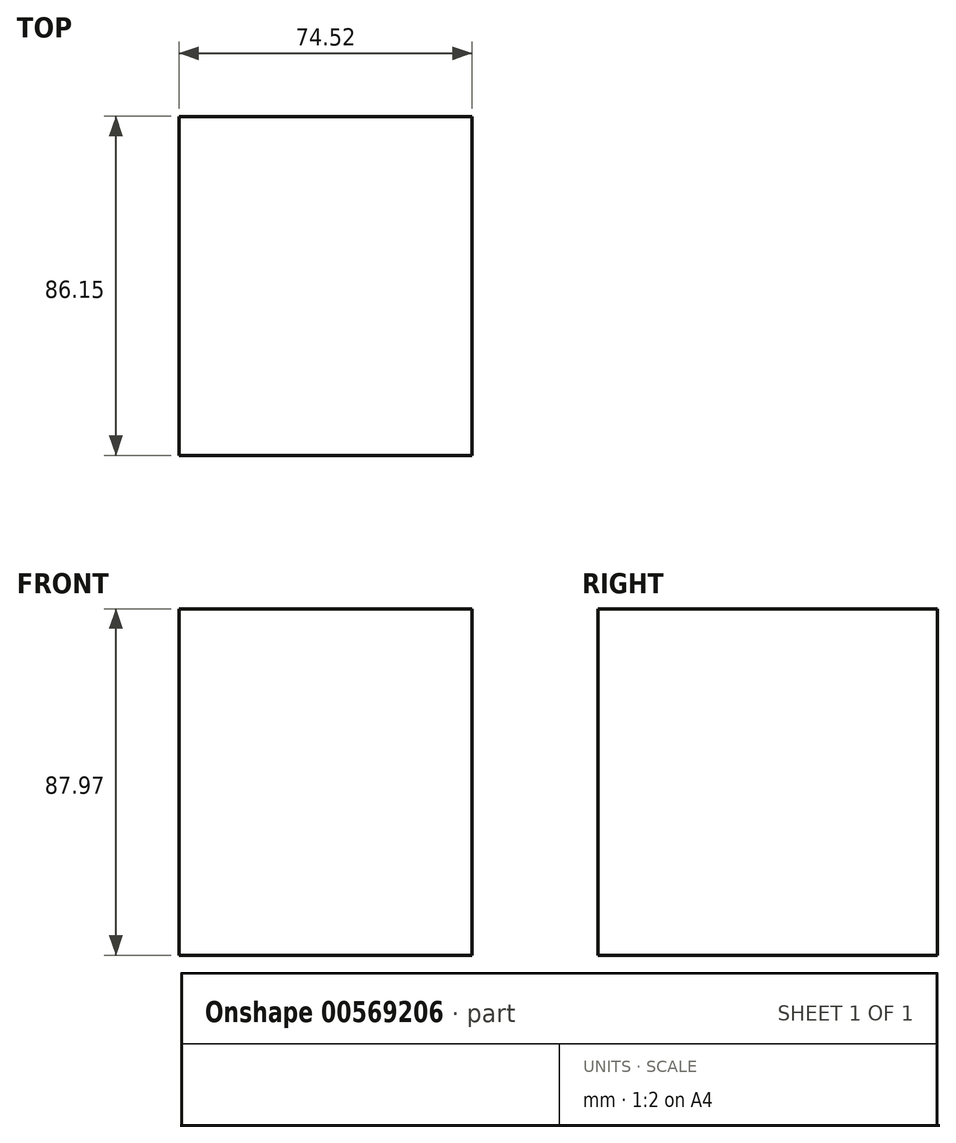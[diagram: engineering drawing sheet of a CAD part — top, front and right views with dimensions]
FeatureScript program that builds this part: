
annotation { "Feature Type Name" : "Feature", "Feature Type Description" : "" }
export const myFeature = defineFeature(function(context is Context, id is Id, definition is map)
    precondition{}
    {
        {
            var Q0;
            Q0=qCreatedBy(makeId("Top.planeOp"),FACE);
            var sketch = newSketch(context, id + "F0", { "sketchPlane" : qUnion([Q0])});
            skLineSegment(sketch, "E0.bottom", {"start": v(-27.12, 33.3) * mm, "end": v(47.4, 33.3) * mm});
            skLineSegment(sketch, "E0.top", {"start": v(-27.12, -52.84) * mm, "end": v(47.4, -52.84) * mm});
            skLineSegment(sketch, "E0.left", {"start": v(-27.12, 33.3) * mm, "end": v(-27.12, -52.84) * mm});
            skLineSegment(sketch, "E0.right", {"start": v(47.4, 33.3) * mm, "end": v(47.4, -52.84) * mm});
            skSolve(sketch);
        }
        {
            var Q0;
            Q0 = qSketchRegion(id + "F0", true);
            extrude(context, id + "F1", {"entities" : qUnion([Q0]), "depth" : 87.97 * mm, "offsetDistance" : 25.4 * mm});
        }
    });
